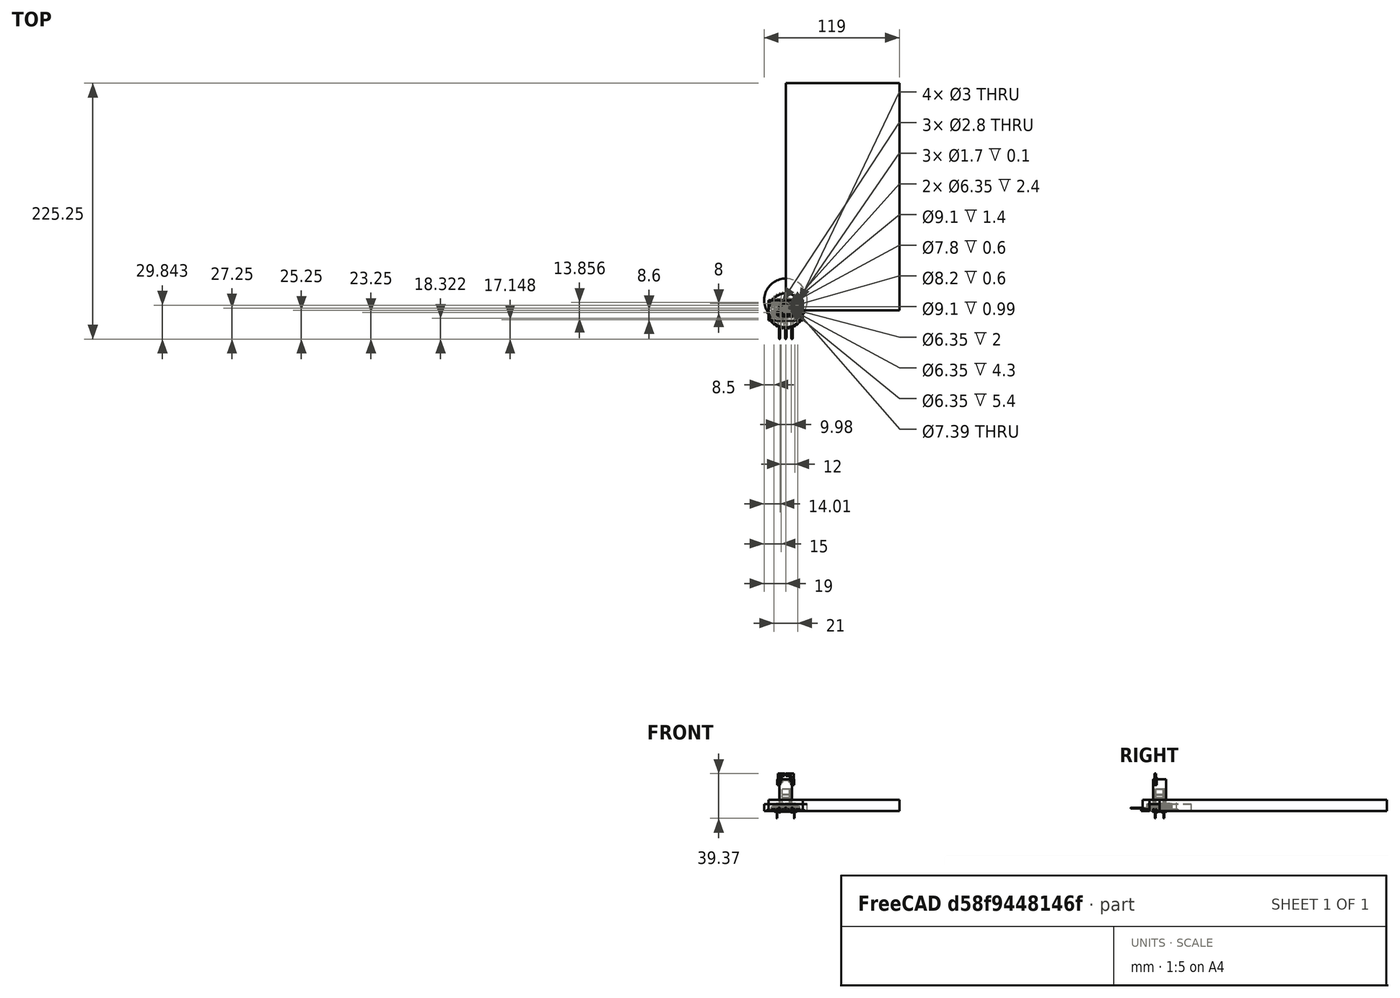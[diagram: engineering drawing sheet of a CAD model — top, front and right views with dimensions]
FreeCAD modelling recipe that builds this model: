
FCSTD DOCUMENT  (FreeCAD 0.18R16033 (Git))
Label: assembly
License: All rights reserved
LicenseURL: http://en.wikipedia.org/wiki/All_rights_reserved
objects: Part::Cylinder×56, Part::Cut×14, Part::FeaturePython×13, Part::MultiFuse×12, Drawing::FeatureViewPython×11, Part::Feature×10, Part::Box×8, Part::Fillet×6, Part::Part2DObjectPython×2, Part::Extrusion×2, Spreadsheet::Sheet×1, Drawing::FeatureViewPart×1, Drawing::FeaturePage×1, App::Part×1
note: 123 computed .brp shape members not serialized (recipe doc carries the construction recipe); baked Part::Feature solids carry a one-line shape summary decoded from their .brp

FEATURE [Part::Cylinder] Cylinder  label="Inner radius"
  Angle = 360
  AttacherType = Attacher::AttachEngine3D
  Height = 25
  Radius = 3.175
  expr: Radius = 6.35 / 2
FEATURE [Part::Cylinder] Cylinder001  label="Extractor"
  Angle = 360
  AttacherType = Attacher::AttachEngine3D
  Height = 2.2
  Radius = 4.5
FEATURE [Part::Cut] Cut002
  Placement = pos=(-0.0122421,-4.00609,26.9908) rot=(0.00162,0.706566,0.707645;3.14051rad)
FEATURE [Part::Cylinder] Cylinder003
  Angle = 360
  AttacherType = Attacher::AttachEngine3D
  Height = 2
  Placement = pos=(0,0,2.5) rot=(1,0,0;0rad)
  Radius = 2
FEATURE [Spreadsheet::Sheet] Spreadsheet  label="Sizes"
  cells = A1=Einzel OD; B1=; A2=Einzel ID; A3=Immersion aperture ID; A4=Einzel 3 Radius; A5=Accelerator
FEATURE [Part::Cylinder] Cylinder004  label="Einzel1"
  Angle = 360
  AttacherType = Attacher::AttachEngine3D
  Height = 2.4
  Placement = pos=(0,0,2.8) rot=(1,0,0;0rad)
  Radius = 4.5
FEATURE [Part::Cylinder] Cylinder005  label="Einzel002"
  Angle = 360
  AttacherType = Attacher::AttachEngine3D
  Height = 5.4
  Placement = pos=(0,0,5.8) rot=(1,0,0;0rad)
  Radius = 4.5
FEATURE [Part::Cylinder] Cylinder006  label="Einzel003"
  Angle = 360
  AttacherType = Attacher::AttachEngine3D
  Height = 2.4
  Placement = pos=(0,0,11.8) rot=(1,0,0;0rad)
  Radius = 4.5
FEATURE [Part::Cylinder] Cylinder007  label="Einzel004"
  Angle = 360
  AttacherType = Attacher::AttachEngine3D
  Height = 4.8
  Placement = pos=(0,0,14.8) rot=(1,0,0;0rad)
  Radius = 4.5
FEATURE [Part::Cylinder] Cylinder008  label="ApertureDisc1"
  Angle = 360
  AttacherType = Attacher::AttachEngine3D
  Height = 0.2
  Placement = pos=(0,0,2) rot=(1,0,0;0rad)
  Radius = 4.5
FEATURE [Part::Cylinder] Cylinder009  label="Aperture1"
  Angle = 360
  AttacherType = Attacher::AttachEngine3D
  Height = 25
  Radius = 0.65
FEATURE [Part::Cylinder] Cylinder010  label="ApertureDisc002"
  Angle = 360
  AttacherType = Attacher::AttachEngine3D
  Height = 0.5
  Placement = pos=(0,0,19.1) rot=(1,0,0;0rad)
  Radius = 4.5
FEATURE [Part::Cylinder] Cylinder011  label="Aperture002"
  Angle = 360
  AttacherType = Attacher::AttachEngine3D
  Height = 25
  Placement = pos=(0,0,10) rot=(0,0,1;0rad)
  Radius = 2.5
FEATURE [Part::MultiFuse] Fusion
  Shapes = -> [Cylinder001,Cylinder003,Cylinder004,Cylinder005,Cylinder006,Cylinder007]
FEATURE [Part::Cut] Cut
  Base = -> Cylinder008
  Tool = -> Cylinder009
FEATURE [Part::Cut] Cut003
  Base = -> Cylinder010
  Tool = -> Cylinder011
FEATURE [Part::Cut] Cut004
  Base = -> Fusion
  Tool = -> Cylinder
FEATURE [Part::MultiFuse] Fusion001
  Shapes = -> [Cut004,Cut003,Cut]
FEATURE [Drawing::FeatureViewPart] Ortho  label="Ortho_0_0"
  Direction = (1,0,0)
  HiddenWidth = 0.35
  LineWidth = 0.35
  Rotation = -90
  Scale = 10
  ShowHiddenLines = true
  ShowSmoothLines = false
  Source = -> Fusion001
  Tolerance = 0.05
  ViewResult = <blob: 24351 chars omitted>
  Visible = true
  X = 115
  Y = 246.5
FEATURE [Drawing::FeatureViewPython] dim001  # drawing view (typed FeaturePython)
  Rotation = 0
  ViewResult = <g> \n  <line x1="162.000000" y1="134.500000" x2="174.066838" y2="134.500000" style="stroke:rgb(0,0,255);stroke-width:0.50" />\n<line x1="162.000000" y1="188.500000" x2="174.066838" y2="188.500000" style="stroke:rgb(0,0,255);stroke-width:0.50" />\n<line x1="173.066838" y1="134.500000" x2="173.066838" y2="188.500000" style="stroke:rgb(0,0,255);stroke-width:0.50" /> \n  <polygon points="173.066838,188.500000 174.066838,185.500000 173.066838,184.500000 172.066838,185.500000" style="fill:rgb(0,0,255);stroke:rgb(0,0,255);stroke-width:0" /><polygon points="173.066838,134.500000 172.066838,137.500000 173.066838,138.500000 174.066838,137.500000" style="fill:rgb(0,0,255);stroke:rgb(0,0,255);stroke-width:0" /> \n  <text x="171.066838" y="161.500000" font-family="inherit" font-size="3.6" fill="rgb(0,0,255)" text-anchor="middle" transform="rotate(-90.000000 171.066838,161.500000)" >5.4</text> </g>
  Visible = true
  X = 0
  Y = 0
  arrowL1 = 3
  arrowL2 = 1
  arrowW = 2
  arrow_scheme = 0
  autoPlaceOffset = 2
  autoPlaceText = true
  click1_x = 173.067
  click1_y = 179.381
  click2_x = 173.067
  click2_y = 179.381
  comma_decimal_place = false
  dimension_line_overshoot = 1
  gap_datum_points = 2
  halfDimension_linear = false
  lineColor = rgb(0,0,255)
  strokeWidth = 0.5
  textFormat_linear = %(value)3.3f
  textRenderer_color = rgb(0,0,255)
  textRenderer_family = inherit
  textRenderer_size = 3.6
  unit_custom_scale = 1
  unit_scheme = 0
FEATURE [Drawing::FeatureViewPython] dim002  # drawing view (typed FeaturePython)
  Rotation = 0
  ViewResult = <g> \n  <line x1="162.000000" y1="218.500000" x2="173.937973" y2="218.500000" style="stroke:rgb(0,0,255);stroke-width:0.50" />\n<line x1="162.000000" y1="194.500000" x2="173.937973" y2="194.500000" style="stroke:rgb(0,0,255);stroke-width:0.50" />\n<line x1="172.937973" y1="218.500000" x2="172.937973" y2="194.500000" style="stroke:rgb(0,0,255);stroke-width:0.50" /> \n  <polygon points="172.937973,194.500000 171.937973,197.500000 172.937973,198.500000 173.937973,197.500000" style="fill:rgb(0,0,255);stroke:rgb(0,0,255);stroke-width:0" /><polygon points="172.937973,218.500000 173.937973,215.500000 172.937973,214.500000 171.937973,215.500000" style="fill:rgb(0,0,255);stroke:rgb(0,0,255);stroke-width:0" /> \n  <text x="170.937973" y="206.500000" font-family="inherit" font-size="3.6" fill="rgb(0,0,255)" text-anchor="middle" transform="rotate(-90.000000 170.937973,206.500000)" >2.4</text> </g>
  Visible = true
  X = 0
  Y = 0
  arrowL1 = 3
  arrowL2 = 1
  arrowW = 2
  arrow_scheme = 0
  autoPlaceOffset = 2
  autoPlaceText = true
  click1_x = 172.938
  click1_y = 197.68
  click2_x = 172.938
  click2_y = 197.68
  comma_decimal_place = false
  dimension_line_overshoot = 1
  gap_datum_points = 2
  halfDimension_linear = false
  lineColor = rgb(0,0,255)
  strokeWidth = 0.5
  textFormat_linear = %(value)3.3f
  textRenderer_color = rgb(0,0,255)
  textRenderer_family = inherit
  textRenderer_size = 3.6
  unit_custom_scale = 1
  unit_scheme = 0
FEATURE [Drawing::FeatureViewPython] dim003  # drawing view (typed FeaturePython)
  Rotation = 0
  ViewResult = <g> \n  <line x1="144.750000" y1="226.500000" x2="135.627725" y2="226.500000" style="stroke:rgb(0,0,255);stroke-width:0.50" />\n<line x1="144.750000" y1="246.500000" x2="135.627725" y2="246.500000" style="stroke:rgb(0,0,255);stroke-width:0.50" />\n<line x1="136.627725" y1="226.500000" x2="136.627725" y2="246.500000" style="stroke:rgb(0,0,255);stroke-width:0.50" /> \n  <polygon points="136.627725,246.500000 137.627725,243.500000 136.627725,242.500000 135.627725,243.500000" style="fill:rgb(0,0,255);stroke:rgb(0,0,255);stroke-width:0" /><polygon points="136.627725,226.500000 135.627725,229.500000 136.627725,230.500000 137.627725,229.500000" style="fill:rgb(0,0,255);stroke:rgb(0,0,255);stroke-width:0" /> \n  <text x="134.627725" y="236.500000" font-family="inherit" font-size="3.6" fill="rgb(0,0,255)" text-anchor="middle" transform="rotate(-90.000000 134.627725,236.500000)" >2</text> </g>
  Visible = true
  X = 0
  Y = 0
  arrowL1 = 3
  arrowL2 = 1
  arrowW = 2
  arrow_scheme = 0
  autoPlaceOffset = 2
  autoPlaceText = true
  click1_x = 136.628
  click1_y = 243.353
  click2_x = 136.628
  click2_y = 243.353
  comma_decimal_place = false
  dimension_line_overshoot = 1
  gap_datum_points = 2
  halfDimension_linear = false
  lineColor = rgb(0,0,255)
  strokeWidth = 0.5
  textFormat_linear = %(value)3.3f
  textRenderer_color = rgb(0,0,255)
  textRenderer_family = inherit
  textRenderer_size = 3.6
  unit_custom_scale = 1
  unit_scheme = 0
FEATURE [Drawing::FeatureViewPython] dim004  # drawing view (typed FeaturePython)
  Rotation = 0
  ViewResult = <g> \n  <line x1="83.250000" y1="96.500000" x2="83.250000" y2="28.362417" style="stroke:rgb(0,0,255);stroke-width:0.50" />\n<line x1="146.750000" y1="96.500000" x2="146.750000" y2="28.362417" style="stroke:rgb(0,0,255);stroke-width:0.50" />\n<line x1="83.250000" y1="29.362417" x2="146.750000" y2="29.362417" style="stroke:rgb(0,0,255);stroke-width:0.50" /> \n  <polygon points="146.750000,29.362417 143.750000,28.362417 142.750000,29.362417 143.750000,30.362417" style="fill:rgb(0,0,255);stroke:rgb(0,0,255);stroke-width:0" /><polygon points="83.250000,29.362417 86.250000,30.362417 87.250000,29.362417 86.250000,28.362417" style="fill:rgb(0,0,255);stroke:rgb(0,0,255);stroke-width:0" /> \n  <text x="115.000000" y="27.362417" font-family="inherit" font-size="3.6" fill="rgb(0,0,255)" text-anchor="middle" transform="rotate(0.000000 115.000000,27.362417)" >6.35</text> </g>
  Visible = true
  X = 0
  Y = 0
  arrowL1 = 3
  arrowL2 = 1
  arrowW = 2
  arrow_scheme = 0
  autoPlaceOffset = 2
  autoPlaceText = true
  click1_x = 135.519
  click1_y = 29.3624
  click2_x = 135.519
  click2_y = 29.3624
  comma_decimal_place = false
  dimension_line_overshoot = 1
  gap_datum_points = 2
  halfDimension_linear = false
  lineColor = rgb(0,0,255)
  strokeWidth = 0.5
  textFormat_linear = %(value)3.3f
  textRenderer_color = rgb(0,0,255)
  textRenderer_family = inherit
  textRenderer_size = 3.6
  unit_custom_scale = 1
  unit_scheme = 0
FEATURE [Drawing::FeatureViewPython] dim005  # drawing view (typed FeaturePython)
  Rotation = 0
  ViewResult = <g> \n  <line x1="90.000000" y1="48.500000" x2="90.000000" y2="42.334978" style="stroke:rgb(0,0,255);stroke-width:0.50" />\n<line x1="140.000000" y1="48.500000" x2="140.000000" y2="42.334978" style="stroke:rgb(0,0,255);stroke-width:0.50" />\n<line x1="90.000000" y1="43.334978" x2="140.000000" y2="43.334978" style="stroke:rgb(0,0,255);stroke-width:0.50" /> \n  <polygon points="140.000000,43.334978 137.000000,42.334978 136.000000,43.334978 137.000000,44.334978" style="fill:rgb(0,0,255);stroke:rgb(0,0,255);stroke-width:0" /><polygon points="90.000000,43.334978 93.000000,44.334978 94.000000,43.334978 93.000000,42.334978" style="fill:rgb(0,0,255);stroke:rgb(0,0,255);stroke-width:0" /> \n  <text x="115.000000" y="41.334978" font-family="inherit" font-size="3.6" fill="rgb(0,0,255)" text-anchor="middle" transform="rotate(0.000000 115.000000,41.334978)" >5</text> </g>
  Visible = true
  X = 0
  Y = 0
  arrowL1 = 3
  arrowL2 = 1
  arrowW = 2
  arrow_scheme = 0
  autoPlaceOffset = 2
  autoPlaceText = true
  click1_x = 137.942
  click1_y = 43.335
  click2_x = 137.942
  click2_y = 43.335
  comma_decimal_place = false
  dimension_line_overshoot = 1
  gap_datum_points = 2
  halfDimension_linear = false
  lineColor = rgb(0,0,255)
  strokeWidth = 0.5
  textFormat_linear = %(value)3.3f
  textRenderer_color = rgb(0,0,255)
  textRenderer_family = inherit
  textRenderer_size = 3.6
  unit_custom_scale = 1
  unit_scheme = 0
FEATURE [Drawing::FeatureViewPython] dim006  # drawing view (typed FeaturePython)
  Rotation = 0
  ViewResult = <g> \n  <line x1="162.000000" y1="98.500000" x2="200.443644" y2="98.500000" style="stroke:rgb(0,0,255);stroke-width:0.50" />\n<line x1="162.000000" y1="50.500000" x2="200.443644" y2="50.500000" style="stroke:rgb(0,0,255);stroke-width:0.50" />\n<line x1="199.443644" y1="98.500000" x2="199.443644" y2="50.500000" style="stroke:rgb(0,0,255);stroke-width:0.50" /> \n  <polygon points="199.443644,50.500000 198.443644,53.500000 199.443644,54.500000 200.443644,53.500000" style="fill:rgb(0,0,255);stroke:rgb(0,0,255);stroke-width:0" /><polygon points="199.443644,98.500000 200.443644,95.500000 199.443644,94.500000 198.443644,95.500000" style="fill:rgb(0,0,255);stroke:rgb(0,0,255);stroke-width:0" /> \n  <text x="197.443644" y="74.500000" font-family="inherit" font-size="3.6" fill="rgb(0,0,255)" text-anchor="middle" transform="rotate(-90.000000 197.443644,74.500000)" >4.8</text> </g>
  Visible = true
  X = 0
  Y = 0
  arrowL1 = 3
  arrowL2 = 1
  arrowW = 2
  arrow_scheme = 0
  autoPlaceOffset = 2
  autoPlaceText = true
  click1_x = 199.444
  click1_y = 58.6136
  click2_x = 199.444
  click2_y = 58.6136
  comma_decimal_place = false
  dimension_line_overshoot = 1
  gap_datum_points = 2
  halfDimension_linear = false
  lineColor = rgb(0,0,255)
  strokeWidth = 0.5
  textFormat_linear = %(value)3.3f
  textRenderer_color = rgb(0,0,255)
  textRenderer_family = inherit
  textRenderer_size = 3.6
  unit_custom_scale = 1
  unit_scheme = 0
FEATURE [Drawing::FeatureViewPython] dim007  # drawing view (typed FeaturePython)
  Rotation = 0
  ViewResult = <g> \n  <line x1="162.000000" y1="128.500000" x2="175.005072" y2="128.500000" style="stroke:rgb(0,0,255);stroke-width:0.50" />\n<line x1="162.000000" y1="104.500000" x2="175.005072" y2="104.500000" style="stroke:rgb(0,0,255);stroke-width:0.50" />\n<line x1="174.005072" y1="128.500000" x2="174.005072" y2="104.500000" style="stroke:rgb(0,0,255);stroke-width:0.50" /> \n  <polygon points="174.005072,104.500000 173.005072,107.500000 174.005072,108.500000 175.005072,107.500000" style="fill:rgb(0,0,255);stroke:rgb(0,0,255);stroke-width:0" /><polygon points="174.005072,128.500000 175.005072,125.500000 174.005072,124.500000 173.005072,125.500000" style="fill:rgb(0,0,255);stroke:rgb(0,0,255);stroke-width:0" /> \n  <text x="172.005072" y="116.500000" font-family="inherit" font-size="3.6" fill="rgb(0,0,255)" text-anchor="middle" transform="rotate(-90.000000 172.005072,116.500000)" >2.4</text> </g>
  Visible = true
  X = 0
  Y = 0
  arrowL1 = 3
  arrowL2 = 1
  arrowW = 2
  arrow_scheme = 0
  autoPlaceOffset = 2
  autoPlaceText = true
  click1_x = 174.005
  click1_y = 110.933
  click2_x = 174.005
  click2_y = 110.933
  comma_decimal_place = false
  dimension_line_overshoot = 1
  gap_datum_points = 2
  halfDimension_linear = false
  lineColor = rgb(0,0,255)
  strokeWidth = 0.5
  textFormat_linear = %(value)3.3f
  textRenderer_color = rgb(0,0,255)
  textRenderer_family = inherit
  textRenderer_size = 3.6
  unit_custom_scale = 1
  unit_scheme = 0
FEATURE [Drawing::FeatureViewPython] dim008  # drawing view (typed FeaturePython)
  Rotation = 0
  ViewResult = <g> \n  <line x1="162.000000" y1="55.500000" x2="179.122449" y2="55.500000" style="stroke:rgb(0,0,255);stroke-width:0.50" />\n<line x1="162.000000" y1="98.500000" x2="179.122449" y2="98.500000" style="stroke:rgb(0,0,255);stroke-width:0.50" />\n<line x1="178.122449" y1="55.500000" x2="178.122449" y2="98.500000" style="stroke:rgb(0,0,255);stroke-width:0.50" /> \n  <polygon points="178.122449,98.500000 179.122449,95.500000 178.122449,94.500000 177.122449,95.500000" style="fill:rgb(0,0,255);stroke:rgb(0,0,255);stroke-width:0" /><polygon points="178.122449,55.500000 177.122449,58.500000 178.122449,59.500000 179.122449,58.500000" style="fill:rgb(0,0,255);stroke:rgb(0,0,255);stroke-width:0" /> \n  <text x="176.122449" y="77.000000" font-family="inherit" font-size="3.6" fill="rgb(0,0,255)" text-anchor="middle" transform="rotate(-90.000000 176.122449,77.000000)" >4.3</text> </g>
  Visible = true
  X = 0
  Y = 0
  arrowL1 = 3
  arrowL2 = 1
  arrowW = 2
  arrow_scheme = 0
  autoPlaceOffset = 2
  autoPlaceText = true
  click1_x = 178.122
  click1_y = 96.6141
  click2_x = 178.122
  click2_y = 96.6141
  comma_decimal_place = false
  dimension_line_overshoot = 1
  gap_datum_points = 2
  halfDimension_linear = false
  lineColor = rgb(0,0,255)
  strokeWidth = 0.5
  textFormat_linear = %(value)3.3f
  textRenderer_color = rgb(0,0,255)
  textRenderer_family = inherit
  textRenderer_size = 3.6
  unit_custom_scale = 1
  unit_scheme = 0
FEATURE [Drawing::FeatureViewPython] dim009  # drawing view (typed FeaturePython)
  Rotation = 0
  ViewResult = <g> \n  <line x1="162.000000" y1="246.500000" x2="174.214586" y2="246.500000" style="stroke:rgb(0,0,255);stroke-width:0.50" />\n<line x1="162.000000" y1="224.500000" x2="174.214586" y2="224.500000" style="stroke:rgb(0,0,255);stroke-width:0.50" />\n<line x1="173.214586" y1="246.500000" x2="173.214586" y2="224.500000" style="stroke:rgb(0,0,255);stroke-width:0.50" /> \n  <polygon points="173.214586,224.500000 172.214586,227.500000 173.214586,228.500000 174.214586,227.500000" style="fill:rgb(0,0,255);stroke:rgb(0,0,255);stroke-width:0" /><polygon points="173.214586,246.500000 174.214586,243.500000 173.214586,242.500000 172.214586,243.500000" style="fill:rgb(0,0,255);stroke:rgb(0,0,255);stroke-width:0" /> \n  <text x="171.214586" y="235.500000" font-family="inherit" font-size="3.6" fill="rgb(0,0,255)" text-anchor="middle" transform="rotate(-90.000000 171.214586,235.500000)" >2.2</text> </g>
  Visible = true
  X = 0
  Y = 0
  arrowL1 = 3
  arrowL2 = 1
  arrowW = 2
  arrow_scheme = 0
  autoPlaceOffset = 2
  autoPlaceText = true
  click1_x = 173.215
  click1_y = 228.125
  click2_x = 173.215
  click2_y = 228.125
  comma_decimal_place = false
  dimension_line_overshoot = 1
  gap_datum_points = 2
  halfDimension_linear = false
  lineColor = rgb(0,0,255)
  strokeWidth = 0.5
  textFormat_linear = %(value)3.3f
  textRenderer_color = rgb(0,0,255)
  textRenderer_family = inherit
  textRenderer_size = 3.6
  unit_custom_scale = 1
  unit_scheme = 0
FEATURE [Drawing::FeatureViewPython] dim010  # drawing view (typed FeaturePython)
  Rotation = 0
  ViewResult = <g> \n  <line x1="108.540870" y1="222.500000" x2="108.540870" y2="222.438451" style="stroke:rgb(0,0,255);stroke-width:0.50" />\n<line x1="108.500000" y1="222.500000" x2="108.500000" y2="222.438451" style="stroke:rgb(0,0,255);stroke-width:0.50" />\n<line x1="108.540870" y1="223.438451" x2="108.500000" y2="223.438451" style="stroke:rgb(0,0,255);stroke-width:0.50" /> \n  <polygon points="108.500000,223.438451 105.500000,222.438451 104.500000,223.438451 105.500000,224.438451" style="fill:rgb(0,0,255);stroke:rgb(0,0,255);stroke-width:0" /><polygon points="108.540870,223.438451 111.540870,224.438451 112.540870,223.438451 111.540870,222.438451" style="fill:rgb(0,0,255);stroke:rgb(0,0,255);stroke-width:0" /> \n  <text x="108.520435" y="221.438451" font-family="inherit" font-size="3.6" fill="rgb(0,0,255)" text-anchor="middle" transform="rotate(-0.000000 108.520435,221.438451)" >0.004</text> </g>
  Visible = true
  X = 0
  Y = 0
  arrowL1 = 3
  arrowL2 = 1
  arrowW = 2
  arrow_scheme = 0
  autoPlaceOffset = 2
  autoPlaceText = true
  click1_x = 108.659
  click1_y = 223.438
  click2_x = 108.659
  click2_y = 223.438
  comma_decimal_place = false
  dimension_line_overshoot = 1
  gap_datum_points = 2
  halfDimension_linear = false
  lineColor = rgb(0,0,255)
  strokeWidth = 0.5
  textFormat_linear = %(value)3.3f
  textRenderer_color = rgb(0,0,255)
  textRenderer_family = inherit
  textRenderer_size = 3.6
  unit_custom_scale = 1
  unit_scheme = 0
FEATURE [Drawing::FeatureViewPython] dim011  # drawing view (typed FeaturePython)
  Rotation = 0
  ViewResult = <g> \n  <line x1="108.500000" y1="226.500000" x2="108.500000" y2="236.513119" style="stroke:rgb(0,0,255);stroke-width:0.50" />\n<line x1="121.500000" y1="226.500000" x2="121.500000" y2="236.513119" style="stroke:rgb(0,0,255);stroke-width:0.50" />\n<line x1="108.500000" y1="235.513119" x2="121.500000" y2="235.513119" style="stroke:rgb(0,0,255);stroke-width:0.50" /> \n  <polygon points="121.500000,235.513119 118.500000,234.513119 117.500000,235.513119 118.500000,236.513119" style="fill:rgb(0,0,255);stroke:rgb(0,0,255);stroke-width:0" /><polygon points="108.500000,235.513119 111.500000,236.513119 112.500000,235.513119 111.500000,234.513119" style="fill:rgb(0,0,255);stroke:rgb(0,0,255);stroke-width:0" /> \n  <text x="115.000000" y="233.513119" font-family="inherit" font-size="3.6" fill="rgb(0,0,255)" text-anchor="middle" transform="rotate(0.000000 115.000000,233.513119)" >1.3</text> </g>
  Visible = true
  X = 0
  Y = 0
  arrowL1 = 3
  arrowL2 = 1
  arrowW = 2
  arrow_scheme = 0
  autoPlaceOffset = 2
  autoPlaceText = true
  click1_x = 117.806
  click1_y = 235.513
  click2_x = 117.806
  click2_y = 235.513
  comma_decimal_place = false
  dimension_line_overshoot = 1
  gap_datum_points = 2
  halfDimension_linear = false
  lineColor = rgb(0,0,255)
  strokeWidth = 0.5
  textFormat_linear = %(value)3.3f
  textRenderer_color = rgb(0,0,255)
  textRenderer_family = inherit
  textRenderer_size = 3.6
  unit_custom_scale = 1
  unit_scheme = 0
FEATURE [Drawing::FeaturePage] Page
  EditableTexts = AUTHOR NAME | CREATION DATE | SUPERVISOR NAME | CHECK DATE | SCALE | WEIGHT | NUMBER | SHEET | TITLE | SUBTITLE
  Group = -> [Ortho,dim001,dim002,dim003,dim004,dim005,dim006,dim007,dim008,dim009,dim010,dim011]
  Template = <path>//share/freecad-daily/Mod/Drawing/Templates/A3_Landscape.svg
FEATURE [Part::Cylinder] Cylinder012  label="Inner radius001"
  Angle = 360
  AttacherType = Attacher::AttachEngine3D
  Height = 25
  Radius = 3.175
  expr: Radius = 6.35 / 2
FEATURE [Part::Cylinder] Cylinder013  label="Extractor001"
  Angle = 360
  AttacherType = Attacher::AttachEngine3D
  Height = 2.2
  Radius = 4.5
FEATURE [Part::Cylinder] Cylinder014  label="Einzel005"
  Angle = 360
  AttacherType = Attacher::AttachEngine3D
  Height = 5.4
  Placement = pos=(0,0,5.8) rot=(1,0,0;0rad)
  Radius = 4.5
FEATURE [Part::Cylinder] Cylinder015
  Angle = 360
  AttacherType = Attacher::AttachEngine3D
  Height = 2
  Placement = pos=(0,0,2.5) rot=(1,0,0;0rad)
  Radius = 2
FEATURE [Part::Cylinder] Cylinder016  label="Aperture003"
  Angle = 360
  AttacherType = Attacher::AttachEngine3D
  Height = 25
  Radius = 0.65
FEATURE [Part::Cylinder] Cylinder017  label="ApertureDisc003"
  Angle = 360
  AttacherType = Attacher::AttachEngine3D
  Height = 0.5
  Placement = pos=(0,0,19.1) rot=(1,0,0;0rad)
  Radius = 4.5
FEATURE [Part::Cylinder] Cylinder018  label="ApertureDisc004"
  Angle = 360
  AttacherType = Attacher::AttachEngine3D
  Height = 0.2
  Placement = pos=(0,0,2) rot=(1,0,0;0rad)
  Radius = 4.5
FEATURE [Part::Cylinder] Cylinder019  label="Aperture004"
  Angle = 360
  AttacherType = Attacher::AttachEngine3D
  Height = 25
  Placement = pos=(0,0,10) rot=(0,0,1;0rad)
  Radius = 2.5
FEATURE [Part::Cylinder] Cylinder020  label="Einzel006"
  Angle = 360
  AttacherType = Attacher::AttachEngine3D
  Height = 4.8
  Placement = pos=(0,0,14.8) rot=(1,0,0;0rad)
  Radius = 4.5
FEATURE [Part::Cylinder] Cylinder021  label="Einzel007"
  Angle = 360
  AttacherType = Attacher::AttachEngine3D
  Height = 2.4
  Placement = pos=(0,0,2.8) rot=(1,0,0;0rad)
  Radius = 4.5
FEATURE [Part::Cylinder] Cylinder022  label="Einzel008"
  Angle = 360
  AttacherType = Attacher::AttachEngine3D
  Height = 2.4
  Placement = pos=(0,0,11.8) rot=(1,0,0;0rad)
  Radius = 4.5
FEATURE [Part::MultiFuse] Fusion002
  Shapes = -> [Cylinder013,Cylinder015,Cylinder021,Cylinder014,Cylinder022,Cylinder020]
FEATURE [Part::Cut] Cut005
  Base = -> Cylinder017
  Tool = -> Cylinder019
FEATURE [Part::Cut] Cut006
  Base = -> Fusion002
  Tool = -> Cylinder012
FEATURE [Part::Cut] Cut007
  Base = -> Cylinder018
  Tool = -> Cylinder016
FEATURE [Part::MultiFuse] Fusion003
  Shapes = -> [Cut006,Cut005,Cut007]
FEATURE [Part::Box] Box  label="Cube"
  AttacherType = Attacher::AttachEngine3D
  Height = 10
  Length = 100
  Width = 200
FEATURE [Part::Cylinder] Cylinder023  label="MountPlateBody"
  Angle = 360
  AttacherType = Attacher::AttachEngine3D
  Height = 1.59
  Radius = 10
FEATURE [Part::Cylinder] Cylinder024  label="Cylinder016"
  Angle = 360
  AttacherType = Attacher::AttachEngine3D
  Height = 10
  Placement = pos=(7,0,0) rot=(0,0,1;0rad)
  Radius = 1.5
FEATURE [Part::FeaturePython] Array  # Draft array (typed FeaturePython)
  Angle = 360
  ArrayType = 1
  Axis = (0,0,1)
  Base = -> Cylinder024
  Center = (0,0,0)
  Fuse = false
  IntervalAxis = (0,0,0)
  IntervalX = (1,0,0)
  IntervalY = (0,1,0)
  IntervalZ = (0,0,1)
  NumberPolar = 3
  NumberX = 2
  NumberY = 2
  NumberZ = 1
FEATURE [Part::Cylinder] Cylinder026  label="MountPlateInnerHole"
  Angle = 360
  AttacherType = Attacher::AttachEngine3D
  Height = 10
  Radius = 3.9
FEATURE [Part::Cylinder] Cylinder027  label="MountPlateLip"
  Angle = 360
  AttacherType = Attacher::AttachEngine3D
  Height = 10
  Placement = pos=(0,0,0.6) rot=(0,0,1;0rad)
  Radius = 4.55
FEATURE [Part::Cylinder] Cylinder028  label="Cylinder"
  Angle = 360
  AttacherType = Attacher::AttachEngine3D
  Height = 10
  Radius = 2
FEATURE [Part::Cylinder] Cylinder029  label="Cylinder017"
  Angle = 360
  AttacherType = Attacher::AttachEngine3D
  Height = 10
  Placement = pos=(8,0,0) rot=(0,0,1;0rad)
  Radius = 1.4
FEATURE [Part::FeaturePython] Array002  # Draft array (typed FeaturePython)
  Angle = 360
  ArrayType = 1
  Axis = (0,0,1)
  Base = -> Cylinder029
  Center = (0,0,0)
  Fuse = false
  IntervalAxis = (0,0,0)
  IntervalX = (1,0,0)
  IntervalY = (0,1,0)
  IntervalZ = (0,0,1)
  NumberPolar = 3
  NumberX = 2
  NumberY = 2
  NumberZ = 1
FEATURE [Part::Box] Box002  label="Cube002"
  AttacherType = Attacher::AttachEngine3D
  Height = 1.5875
  Length = 10
  Placement = pos=(0.5,-2.5,0) rot=(0,0,1;0rad)
  Width = 5
FEATURE [Part::Fillet] Fillet001
  Base = -> Box002
  Edges = 2 edges r=2: [Edge5,Edge7]
FEATURE [Part::FeaturePython] Array003  # Draft array (typed FeaturePython)
  Angle = 360
  ArrayType = 1
  Axis = (0,0,1)
  Base = -> Fillet001
  Center = (0,0,0)
  Fuse = false
  IntervalAxis = (0,0,0)
  IntervalX = (1,0,0)
  IntervalY = (0,1,0)
  IntervalZ = (0,0,1)
  NumberPolar = 3
  NumberX = 2
  NumberY = 2
  NumberZ = 1
FEATURE [Part::Cylinder] Cylinder030  label="MountPlateLip001"
  Angle = 360
  AttacherType = Attacher::AttachEngine3D
  Height = 10
  Placement = pos=(0,0,0.6) rot=(0,0,1;0rad)
  Radius = 4.55
FEATURE [Part::Cylinder] Cylinder031  label="MountPlateInnerHole001"
  Angle = 360
  AttacherType = Attacher::AttachEngine3D
  Height = 10
  Radius = 4.1
FEATURE [Part::MultiFuse] Fusion006
  Shapes = -> [Cylinder031,Cylinder030,Array002]
FEATURE [Part::Cylinder] Cylinder032  label="MountPlateBody001"
  Angle = 360
  AttacherType = Attacher::AttachEngine3D
  Height = 1.59
  Radius = 7
FEATURE [Part::MultiFuse] Fusion007
  Shapes = -> [Cylinder032,Array003]
FEATURE [Part::Cut] Cut009
  Base = -> Fusion007
  Tool = -> Fusion006
FEATURE [Part::Cylinder] Cylinder035  label="MountPlateBody002"
  Angle = 360
  AttacherType = Attacher::AttachEngine3D
  Height = 3
  Radius = 7
FEATURE [Part::Cylinder] Cylinder036  label="Cylinder020"
  Angle = 360
  AttacherType = Attacher::AttachEngine3D
  Height = 10
  Placement = pos=(8,0,0) rot=(0,0,1;0rad)
  Radius = 1.4
FEATURE [Part::FeaturePython] Array004  # Draft array (typed FeaturePython)
  Angle = 360
  ArrayType = 1
  Axis = (0,0,1)
  Base = -> Cylinder036
  Center = (0,0,0)
  Fuse = false
  IntervalAxis = (0,0,0)
  IntervalX = (1,0,0)
  IntervalY = (0,1,0)
  IntervalZ = (0,0,1)
  NumberPolar = 3
  NumberX = 2
  NumberY = 2
  NumberZ = 1
FEATURE [Part::Cylinder] Cylinder037  label="MountPlateInnerHole002"
  Angle = 360
  AttacherType = Attacher::AttachEngine3D
  Height = 10
  Radius = 3.7
FEATURE [Part::Cylinder] Cylinder038  label="MountPlateLip002"
  Angle = 86
  AttacherType = Attacher::AttachEngine3D
  Height = 10
  Placement = pos=(0,0,0.6) rot=(0,0,1;0rad)
  Radius = 4.7
FEATURE [Part::Box] Box003  label="Cube003"
  AttacherType = Attacher::AttachEngine3D
  Height = 3
  Length = 10
  Placement = pos=(0.5,-2.5,0) rot=(0,0,1;0rad)
  Width = 5
FEATURE [Part::Fillet] Fillet002
  Base = -> Box003
  Edges = 2 edges r=2: [Edge5,Edge7]
FEATURE [Part::FeaturePython] Array005  # Draft array (typed FeaturePython)
  Angle = 360
  ArrayType = 1
  Axis = (0,0,1)
  Base = -> Fillet002
  Center = (0,0,0)
  Fuse = false
  IntervalAxis = (0,0,0)
  IntervalX = (1,0,0)
  IntervalY = (0,1,0)
  IntervalZ = (0,0,1)
  NumberPolar = 3
  NumberX = 2
  NumberY = 2
  NumberZ = 1
FEATURE [Part::Cylinder] Cylinder039  label="Cylinder021"
  Angle = 360
  AttacherType = Attacher::AttachEngine3D
  Height = 3
  Placement = pos=(-7,0,0) rot=(0,0,1;0rad)
  Radius = 2
FEATURE [Part::MultiFuse] Fusion010
  Shapes = -> [Cylinder039,Array005,Cylinder035]
FEATURE [Part::Cylinder] Cylinder040  label="Cylinder022"
  Angle = 360
  AttacherType = Attacher::AttachEngine3D
  Height = 10
  Placement = pos=(-7,0,0) rot=(0,0,1;0rad)
  Radius = 1
  expr: Radius = 1
FEATURE [Part::Cylinder] Cylinder041  label="Cylinder023"
  Angle = 360
  AttacherType = Attacher::AttachEngine3D
  Height = 25
  Placement = pos=(0,0,3) rot=(0,0,1;0rad)
  Radius = 5.58
FEATURE [Part::Fillet] Fillet003
  Base = -> Cylinder038
  Edges = 2 edges r=0.79: [Edge2,Edge4]
FEATURE [Part::FeaturePython] Array006  # Draft array (typed FeaturePython)
  Angle = 360
  ArrayType = 1
  Axis = (0,0,1)
  Base = -> Fillet003
  Center = (0,0,0)
  Fuse = false
  IntervalAxis = (0,0,0)
  IntervalX = (1,0,0)
  IntervalY = (0,1,0)
  IntervalZ = (0,0,1)
  NumberPolar = 4
  NumberX = 2
  NumberY = 2
  NumberZ = 1
FEATURE [Part::MultiFuse] Fusion011
  Shapes = -> [Array004,Cylinder040,Cylinder037,Array006]
FEATURE [Part::Cut] Cut011
  Base = -> Fusion010
  Tool = -> Fusion011
FEATURE [Part::Cylinder] Cylinder042  label="Cylinder024"
  Angle = 360
  AttacherType = Attacher::AttachEngine3D
  Height = 6.5
  Radius = 11
FEATURE [Part::Cut] Cut012
  Base = -> Cylinder042
  Tool = -> Cut011
FEATURE [Part::Cylinder] Cylinder044  label="Cylinder026"
  Angle = 360
  AttacherType = Attacher::AttachEngine3D
  Height = 10
  Placement = pos=(7,0,0) rot=(0,0,1;0rad)
  Radius = 0.8
FEATURE [Part::MultiFuse] Fusion012
  Shapes = -> [Array,Cylinder027,Cylinder026]
FEATURE [Part::Cylinder] Cylinder045  label="MountPlateLip003"
  Angle = 84
  AttacherType = Attacher::AttachEngine3D
  Height = 4.8
  Placement = pos=(0,0,0.6) rot=(0,0,1;0.05236rad)
  Radius = 5.5
FEATURE [Part::Fillet] Fillet004
  Base = -> Cylinder045
  Edges = 2 edges r=0.79: [Edge2,Edge4]
FEATURE [Part::Cylinder] Cylinder046  label="Cylinder027"
  Angle = 360
  AttacherType = Attacher::AttachEngine3D
  Height = 6.5
  Radius = 10
FEATURE [Part::Cylinder] Cylinder048  label="Cylinder028"
  Angle = 360
  AttacherType = Attacher::AttachEngine3D
  Height = 10
  Radius = 1.5
  expr: Radius = 1.5
FEATURE [Part::FeaturePython] Array010  # Draft array (typed FeaturePython)
  Angle = 360
  ArrayType = 0
  Axis = (0,0,1)
  Base = -> Cylinder048
  Center = (0,0,0)
  Fuse = false
  IntervalAxis = (0,0,0)
  IntervalX = (21,0,0)
  IntervalY = (0,8,0)
  IntervalZ = (0,0,1)
  NumberPolar = 4
  NumberX = 2
  NumberY = 2
  NumberZ = 1
  Placement = pos=(-10.5,-4,0) rot=(0,0,1;0rad)
FEATURE [Part::Cylinder] Cylinder049  label="MountPlateInnerHole003"
  Angle = 360
  AttacherType = Attacher::AttachEngine3D
  Height = 10
  Radius = 3.9
FEATURE [Part::Cylinder] Cylinder050  label="MountPlateLip004"
  Angle = 360
  AttacherType = Attacher::AttachEngine3D
  Height = 10
  Placement = pos=(0,0,0.6) rot=(0,0,1;0rad)
  Radius = 4.55
FEATURE [Part::Cylinder] Cylinder051  label="Cylinder049"
  Angle = 360
  AttacherType = Attacher::AttachEngine3D
  Height = 10
  Placement = pos=(7,0,0) rot=(0,0,1;0rad)
  Radius = 0.8
FEATURE [Part::FeaturePython] Array009  # Draft array (typed FeaturePython)
  Angle = 360
  ArrayType = 1
  Axis = (0,0,1)
  Base = -> Cylinder051
  Center = (0,0,0)
  Fuse = false
  IntervalAxis = (0,0,0)
  IntervalX = (1,0,0)
  IntervalY = (0,1,0)
  IntervalZ = (0,0,1)
  NumberPolar = 3
  NumberX = 2
  NumberY = 2
  NumberZ = 1
  Placement = pos=(0,0,0) rot=(0,0,-1;0.785398rad)
FEATURE [Part::FeaturePython] Array008  # Draft array (typed FeaturePython)
  Angle = 360
  ArrayType = 1
  Axis = (0,0,1)
  Base = -> Fillet004
  Center = (0,0,0)
  Fuse = false
  IntervalAxis = (0,0,0)
  IntervalX = (1,0,0)
  IntervalY = (0,1,0)
  IntervalZ = (0,0,1)
  NumberPolar = 4
  NumberX = 2
  NumberY = 2
  NumberZ = 1
FEATURE [Part::Part2DObjectPython] InvoluteGear001  # Draft 2D object (typed FeaturePython)
  ExternalGear = true
  HighPrecision = true
  Modules = 0.85
  NumberOfTeeth = 36
  PressureAngle = 20
FEATURE [Part::Extrusion] Extrude001
  Base = -> InvoluteGear001
  Dir = (0,0,1)
  DirMode = 2
  FaceMakerClass = Part::FaceMakerBullseye
  LengthFwd = 1.59
  LengthRev = 0
  Solid = true
  Symmetric = false
FEATURE [Part::Part2DObjectPython] InvoluteGear  # Draft 2D object (typed FeaturePython)
  ExternalGear = true
  HighPrecision = true
  Modules = 0.85
  NumberOfTeeth = 7
  PressureAngle = 20
FEATURE [Part::Extrusion] Extrude
  Base = -> InvoluteGear
  Dir = (0,0,1)
  DirMode = 2
  FaceMakerClass = Part::FaceMakerBullseye
  LengthFwd = 1.59
  LengthRev = 0
  Solid = true
  Symmetric = false
FEATURE [Part::Cylinder] Cylinder052
  Angle = 360
  AttacherType = Attacher::AttachEngine3D
  Height = 10
  Radius = 15
FEATURE [Part::Cylinder] Cylinder002
  Angle = 360
  AttacherType = Attacher::AttachEngine3D
  Height = 10
  Radius = 0.875
  expr: Radius = 1.75 / 2
FEATURE [Part::Cut] Cut017
  Base = -> Extrude
  Tool = -> Cylinder002
FEATURE [Part::Cylinder] Cylinder055  label="WireWrap"
  Angle = 360
  AttacherType = Attacher::AttachEngine3D
  Height = 10
  Placement = pos=(-5,3.5,0) rot=(0,0,1;0rad)
  Radius = 0.5
  expr: Radius = 0.5
FEATURE [Part::FeaturePython] Array012  # Draft array (typed FeaturePython)
  Angle = 360
  ArrayType = 1
  Axis = (0,0,1)
  Base = -> Cylinder055
  Center = (0,0,0)
  Fuse = false
  IntervalAxis = (0,0,0)
  IntervalX = (1,0,0)
  IntervalY = (0,1,0)
  IntervalZ = (0,0,1)
  NumberPolar = 1
  NumberX = 2
  NumberY = 2
  NumberZ = 1
FEATURE [Part::Cylinder] Cylinder056  label="Wafer"
  Angle = 360
  AttacherType = Attacher::AttachEngine3D
  Height = 6
  Placement = pos=(0,9,0) rot=(0,0,1;0rad)
  Radius = 19
FEATURE [Part::Feature] Part__Feature  label="ACO"
  shape: bbox 20.2 x 12.6 x 10.95 mm, 91 faces (baked)
FEATURE [Part::Feature] Part__Feature001  label="PG-TO247-3-901_LOWER_MOLD"
  shape: bbox 15.58 x 20.21 x 1.995 mm, 30 faces (baked)
FEATURE [Part::Feature] Part__Feature002  label="PG-TO247-3-901_UPPER_MOLD"
  shape: bbox 15.58 x 20.21 x 2.985 mm, 17 faces (baked)
FEATURE [Part::Feature] Part__Feature003  label="PG-TO247-3-901_EXPOSED_PAD_1"
  shape: bbox 13.46 x 13.08 x 0.635 mm, 13 faces (baked)
FEATURE [Part::Feature] Part__Feature004  label="PG-TO247-3-901_EXPOSED_PAD_2"
  shape: bbox 13.58 x 5.005 x 0.635 mm, 12 faces, 2 solids (baked)
FEATURE [Part::Feature] Part__Feature005  label="PG-TO247-3-901_EXPOSED_LEAD_1"
  Placement = pos=(-5.46,-10.1025,2.4) rot=(0,0,1;0rad)
  shape: bbox 2.02 x 15.33 x 0.635 mm, 14 faces (baked)
FEATURE [Part::Feature] Part__Feature006  label="PG-TO247-3-901_EXPOSED_LEAD_2"
  Placement = pos=(0,-10.1025,2.4) rot=(0,0,1;0rad)
  shape: bbox 3.01 x 15.33 x 0.635 mm, 14 faces (baked)
FEATURE [Part::Feature] Part__Feature007  label="PG-TO247-3-901_EXPOSED_LEAD_003"
  Placement = pos=(5.46,-10.1025,2.4) rot=(0,0,1;0rad)
  shape: bbox 2.02 x 15.33 x 0.635 mm, 14 faces (baked)
FEATURE [Part::Feature] Part__Feature008  label="PG-TO247-3-901_LOGO"
  shape: bbox 11 x 2.319 x 0.01002 mm, 217 faces, 12 solids (baked)
FEATURE [App::Part] PG_TO247_3_901  label="PG-TO247-3-901"
  Group = -> [Part__Feature001,Part__Feature002,Part__Feature003,Part__Feature004,Part__Feature005,Part__Feature006,Part__Feature007,Part__Feature008]
  Origin = -> Origin001
FEATURE [Part::Cylinder] Cylinder059  label="MountPlateInnerHole004"
  Angle = 360
  AttacherType = Attacher::AttachEngine3D
  Height = 10
  Radius = 3.9
FEATURE [Part::Cylinder] Cylinder060  label="MountPlateLip005"
  Angle = 360
  AttacherType = Attacher::AttachEngine3D
  Height = 10
  Placement = pos=(0,0,0.6) rot=(0,0,1;0rad)
  Radius = 4.55
FEATURE [Part::Box] Box004  label="Cube004"
  AttacherType = Attacher::AttachEngine3D
  Height = 4
  Length = 25
  Placement = pos=(-12.5,-6,0) rot=(0,0,1;0rad)
  Width = 12
FEATURE [Part::Fillet] Fillet006
  Base = -> Box004
  Edges = 4 edges r=2: [Edge1,Edge3,Edge5,Edge7]
FEATURE [Part::Cylinder] Cylinder061  label="WireWrap001"
  Angle = 360
  AttacherType = Attacher::AttachEngine3D
  Height = 10
  Placement = pos=(6,2,0) rot=(0,0,1;0rad)
  Radius = 0.5
  expr: Radius = 0.5
FEATURE [Part::FeaturePython] Array015  # Draft array (typed FeaturePython)
  Angle = 360
  ArrayType = 1
  Axis = (0,0,1)
  Base = -> Cylinder061
  Center = (0,0,0)
  Fuse = false
  IntervalAxis = (0,0,0)
  IntervalX = (1,0,0)
  IntervalY = (0,1,0)
  IntervalZ = (0,0,1)
  NumberPolar = 4
  NumberX = 2
  NumberY = 2
  NumberZ = 1
  Placement = pos=(0,0,0) rot=(0,0,1;0.488692rad)
FEATURE [Part::MultiFuse] Fusion014
  Shapes = -> [Fusion012,Array012]
FEATURE [Part::Feature] Part__Feature009  label="95412A409"
  Placement = pos=(7,0,5) rot=(0,0,1;1.5708rad)
  shape: bbox 2.914 x 13.19 x 3.364 mm, 48 faces (baked)
FEATURE [Part::Box] Box006  label="Cube006"
  AttacherType = Attacher::AttachEngine3D
  Height = 10
  Length = 3
  Placement = pos=(6.1,-7,2) rot=(0,0,1;0rad)
  Width = 13.9
  expr: Length = 3
FEATURE [Part::Box] Box007  label="Cube007"
  AttacherType = Attacher::AttachEngine3D
  Height = 10
  Length = 3
  Placement = pos=(-9.1,-6,2) rot=(0,0,1;0rad)
  Width = 12.9
  expr: Length = 3
FEATURE [Part::MultiFuse] Fusion019
  Shapes = -> [Array015,Array008,Cylinder049,Array010,Box007,Box006]
FEATURE [Part::Cut] Cut022  label="FrontPlate"
  Base = -> Fillet006
  Tool = -> Fusion019
FEATURE [Part::Cylinder] Cylinder063  label="Cylinder053"
  Angle = 360
  AttacherType = Attacher::AttachEngine3D
  Height = 10
  Radius = 1.5
  expr: Radius = 1.5
FEATURE [Part::FeaturePython] Array018  # Draft array (typed FeaturePython)
  Angle = 360
  ArrayType = 0
  Axis = (0,0,1)
  Base = -> Cylinder063
  Center = (0,0,0)
  Fuse = false
  IntervalAxis = (0,0,0)
  IntervalX = (21,0,0)
  IntervalY = (0,8,0)
  IntervalZ = (0,0,1)
  NumberPolar = 4
  NumberX = 2
  NumberY = 2
  NumberZ = 1
  Placement = pos=(-10.5,-4,0) rot=(0,0,1;0rad)
FEATURE [Part::Cylinder] Cylinder064  label="MountPlateInnerHole005"
  Angle = 360
  AttacherType = Attacher::AttachEngine3D
  Height = 10
  Radius = 3.9
FEATURE [Part::Cylinder] Cylinder065  label="WireWrap002"
  Angle = 360
  AttacherType = Attacher::AttachEngine3D
  Height = 10
  Placement = pos=(6,2,0) rot=(0,0,1;0rad)
  Radius = 0.5
  expr: Radius = 0.5
FEATURE [Part::FeaturePython] Array016  # Draft array (typed FeaturePython)
  Angle = 360
  ArrayType = 1
  Axis = (0,0,1)
  Base = -> Cylinder065
  Center = (0,0,0)
  Fuse = false
  IntervalAxis = (0,0,0)
  IntervalX = (1,0,0)
  IntervalY = (0,1,0)
  IntervalZ = (0,0,1)
  NumberPolar = 4
  NumberX = 2
  NumberY = 2
  NumberZ = 1
  Placement = pos=(0,0,0) rot=(0,0,1;0.488692rad)
FEATURE [Part::MultiFuse] Fusion020
  Shapes = -> [Array018,Array016,Cylinder060,Cylinder059]
FEATURE [Part::Box] Box008  label="Cube008"
  AttacherType = Attacher::AttachEngine3D
  Height = 2
  Length = 25
  Placement = pos=(-12.5,-6,0) rot=(0,0,1;0rad)
  Width = 12
FEATURE [Part::Fillet] Fillet008
  Base = -> Box008
  Edges = 4 edges r=2: [Edge1,Edge3,Edge5,Edge7]
FEATURE [Part::Cut] Cut023  label="BackPlate"
  Base = -> Fillet008
  Placement = pos=(0,2,0) rot=(0,0,1;0rad)
  Tool = -> Fusion020
FEATURE [Part::Box] Box009  label="Cube009"
  AttacherType = Attacher::AttachEngine3D
  Height = 10
  Length = 30
  Placement = pos=(-15,-9,0) rot=(0,0,1;0rad)
  Width = 18
FEATURE [Part::Cut] Cut024
  Base = -> Box009
  Tool = -> Cut022
note: 1 file-system path scrubbed to <path> (originals preserved in the JSON sidecar)
